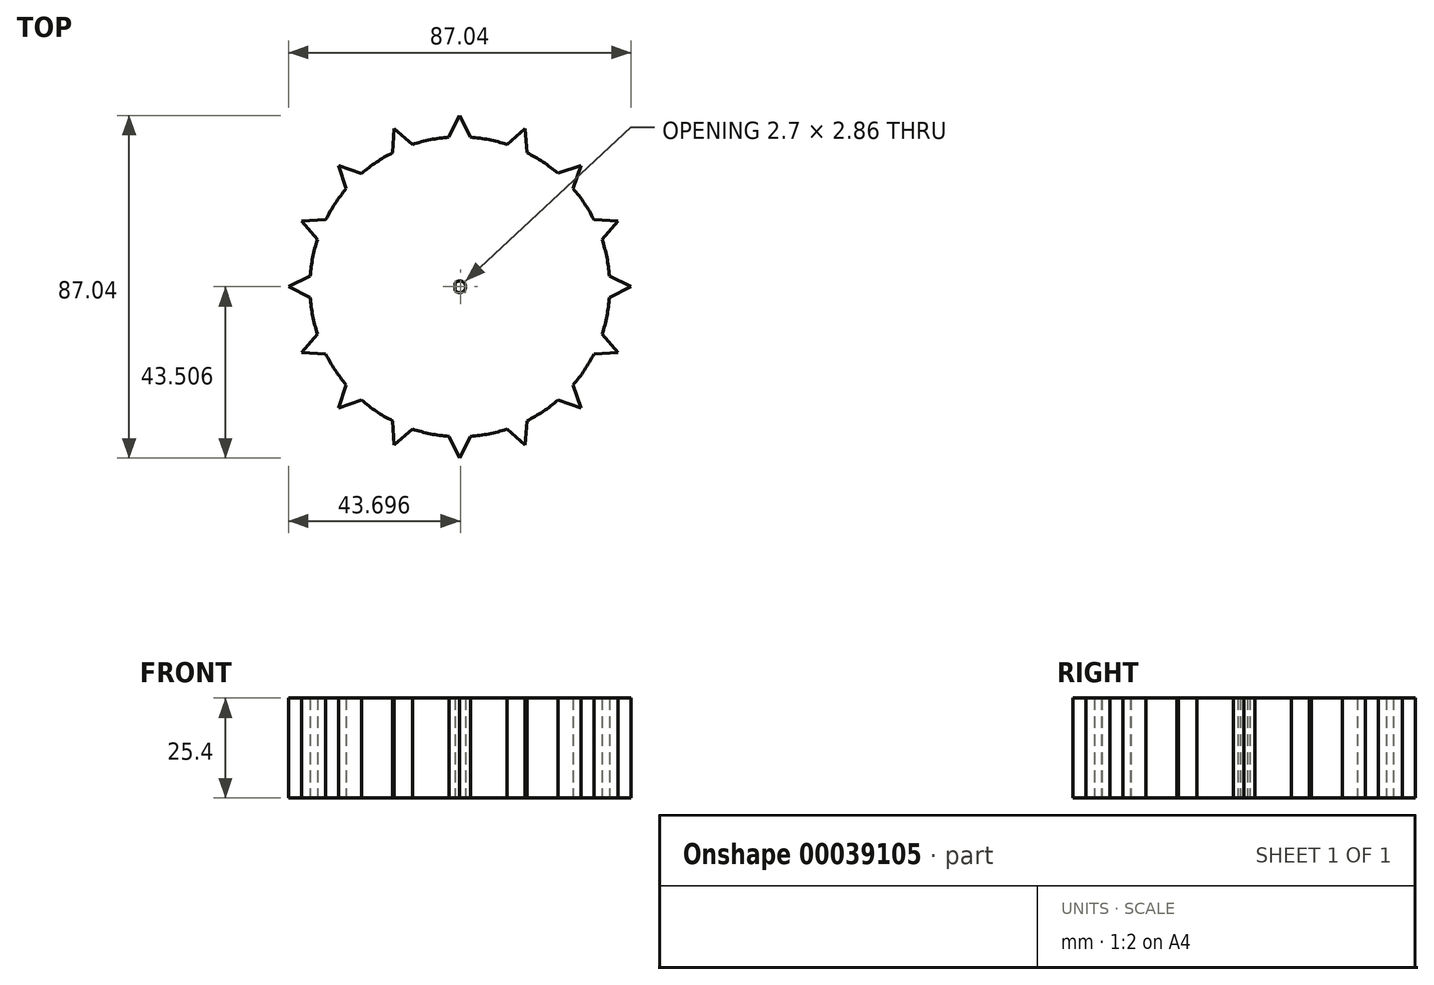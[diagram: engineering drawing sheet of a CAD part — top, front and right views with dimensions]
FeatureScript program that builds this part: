
annotation { "Feature Type Name" : "Feature", "Feature Type Description" : "" }
export const myFeature = defineFeature(function(context is Context, id is Id, definition is map)
    precondition{}
    {
        {
            var Q0;
            Q0=qCreatedBy(makeId("Top.planeOp"),FACE);
            var sketch = newSketch(context, id + "F0", { "sketchPlane" : qUnion([Q0])});
            skArc(sketch, "E0", {"start": v(-1.17, -0.91) * mm, "mid": v(1.53, -0.01) * mm, "end": v(-1.17, 0.89) * mm});
            skLineSegment(sketch, "E1", {"start": v(0, 0) * mm, "end": v(0, 0) * mm});
            skLineSegment(sketch, "E2", {"start": v(-1.17, 0.89) * mm, "end": v(-1.17, -0.91) * mm});
            skArc(sketch, "E3", {"start": v(-17.1, 34.02) * mm, "mid": v(14.62, -35.2) * mm, "end": v(-11.97, 36.15) * mm});
            skLineSegment(sketch, "E4", {"start": v(-2.77, 37.98) * mm, "end": v(0, 43.52) * mm});
            skLineSegment(sketch, "E5", {"start": v(0, 43.52) * mm, "end": v(2.77, 37.99) * mm});
            skLineSegment(sketch, "E6.1.0", {"start": v(-17.1, 34.02) * mm, "end": v(-16.65, 40.2) * mm});
            skLineSegment(sketch, "E6.1.1", {"start": v(-16.65, 40.2) * mm, "end": v(-11.97, 36.15) * mm});
            skLineSegment(sketch, "E6.2.0", {"start": v(-28.08, 22.69) * mm, "end": v(-30.77, 30.77) * mm});
            skLineSegment(sketch, "E6.2.1", {"start": v(-30.77, 30.77) * mm, "end": v(-22.69, 28.08) * mm});
            skLineSegment(sketch, "E6.3.0", {"start": v(-34.62, 10.22) * mm, "end": v(-40.2, 16.65) * mm});
            skLineSegment(sketch, "E6.3.1", {"start": v(-40.2, 16.65) * mm, "end": v(-31.7, 17.26) * mm});
            skLineSegment(sketch, "E6.4.0", {"start": v(-35.9, -3.8) * mm, "end": v(-43.52, 0) * mm});
            skLineSegment(sketch, "E6.4.1", {"start": v(-43.52, 0) * mm, "end": v(-35.9, 3.81) * mm});
            skLineSegment(sketch, "E6.5.0", {"start": v(-31.7, -17.26) * mm, "end": v(-40.2, -16.65) * mm});
            skLineSegment(sketch, "E6.5.1", {"start": v(-40.2, -16.65) * mm, "end": v(-34.62, -10.22) * mm});
            skLineSegment(sketch, "E6.6.0", {"start": v(-22.69, -28.08) * mm, "end": v(-30.77, -30.77) * mm});
            skLineSegment(sketch, "E6.6.1", {"start": v(-30.77, -30.77) * mm, "end": v(-28.08, -22.69) * mm});
            skLineSegment(sketch, "E6.7.0", {"start": v(-10.22, -34.62) * mm, "end": v(-16.65, -40.2) * mm});
            skLineSegment(sketch, "E6.7.1", {"start": v(-16.65, -40.2) * mm, "end": v(-17.26, -31.7) * mm});
            skLineSegment(sketch, "E6.8.0", {"start": v(3.8, -35.9) * mm, "end": v(0, -43.52) * mm});
            skLineSegment(sketch, "E6.8.1", {"start": v(0, -43.52) * mm, "end": v(-3.81, -35.9) * mm});
            skLineSegment(sketch, "E6.9.0", {"start": v(17.26, -31.7) * mm, "end": v(16.65, -40.2) * mm});
            skLineSegment(sketch, "E6.9.1", {"start": v(16.65, -40.2) * mm, "end": v(10.22, -34.62) * mm});
            skLineSegment(sketch, "E6.10.0", {"start": v(28.08, -22.69) * mm, "end": v(30.77, -30.77) * mm});
            skLineSegment(sketch, "E6.10.1", {"start": v(30.77, -30.77) * mm, "end": v(22.69, -28.08) * mm});
            skLineSegment(sketch, "E6.11.0", {"start": v(34.62, -10.22) * mm, "end": v(40.2, -16.65) * mm});
            skLineSegment(sketch, "E6.11.1", {"start": v(40.2, -16.65) * mm, "end": v(31.7, -17.26) * mm});
            skLineSegment(sketch, "E6.12.0", {"start": v(35.9, 3.8) * mm, "end": v(43.52, 0) * mm});
            skLineSegment(sketch, "E6.12.1", {"start": v(43.52, 0) * mm, "end": v(35.9, -3.81) * mm});
            skLineSegment(sketch, "E6.13.0", {"start": v(31.7, 17.26) * mm, "end": v(40.2, 16.65) * mm});
            skLineSegment(sketch, "E6.13.1", {"start": v(40.2, 16.65) * mm, "end": v(34.62, 10.22) * mm});
            skLineSegment(sketch, "E6.14.0", {"start": v(22.69, 28.08) * mm, "end": v(30.77, 30.77) * mm});
            skLineSegment(sketch, "E6.14.1", {"start": v(30.77, 30.77) * mm, "end": v(28.08, 22.69) * mm});
            skLineSegment(sketch, "E6.15.0", {"start": v(11.99, 36.16) * mm, "end": v(16.65, 40.2) * mm});
            skLineSegment(sketch, "E6.15.1", {"start": v(16.65, 40.2) * mm, "end": v(17.1, 34.05) * mm});
            skPoint(sketch, "E6.center", {"position": v(0, 0) * mm});
            skPoint(sketch, "E7.orphan", {"position": v(-17.26, 31.7) * mm});
            skPoint(sketch, "E8.orphan", {"position": v(-10.22, 34.62) * mm});
            skPoint(sketch, "E9.end.orphan", {"position": v(-3.81, 35.9) * mm});
            skPoint(sketch, "E10.orphan", {"position": v(10.22, 34.62) * mm});
            skPoint(sketch, "E11.orphan", {"position": v(17.26, 31.7) * mm});
            skSolve(sketch);
        }
        {
            var Q0;
            Q0 = qSketchRegion(id + "F0", true);
            extrude(context, id + "F1", {"entities" : qUnion([Q0]), "depth" : 25.4 * mm});
        }
    });
